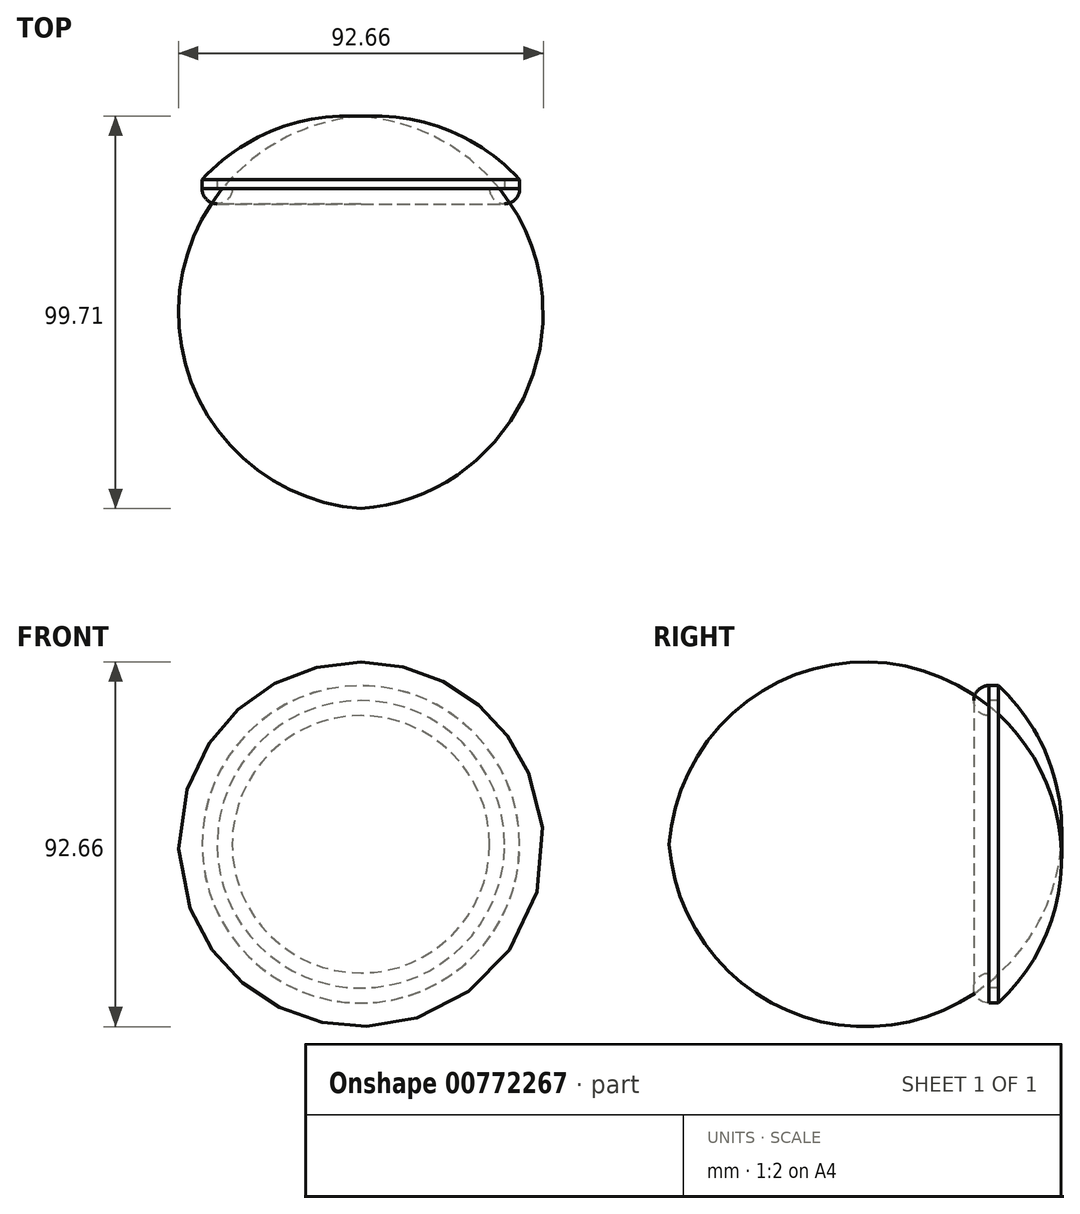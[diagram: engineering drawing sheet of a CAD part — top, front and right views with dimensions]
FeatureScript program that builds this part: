
annotation { "Feature Type Name" : "Feature", "Feature Type Description" : "" }
export const myFeature = defineFeature(function(context is Context, id is Id, definition is map)
    precondition{}
    {
        {
            var Q0;
            Q0=qCreatedBy(makeId("Top.planeOp"),FACE);
            var sketch = newSketch(context, id + "F0", { "sketchPlane" : qUnion([Q0])});
            skLineSegment(sketch, "E0", {"start": v(40.32, 0) * mm, "end": v(0, 0) * mm});
            skLineSegment(sketch, "E1", {"start": v(0, 0) * mm, "end": v(0, 15.98) * mm});
            skArc(sketch, "E2", {"start": v(40.32, 0) * mm, "mid": v(21.98, 12.6) * mm, "end": v(0, 15.98) * mm});
            skLineSegment(sketch, "E3", {"start": v(36.52, 0) * mm, "end": v(36.52, -2.4) * mm});
            skLineSegment(sketch, "E4", {"start": v(36.52, -2.4) * mm, "end": v(32.7, -2.4) * mm});
            skArc(sketch, "E5", {"start": v(32.7, -2.4) * mm, "mid": v(36.52, -6.21) * mm, "end": v(40.34, -2.4) * mm});
            skLineSegment(sketch, "E6", {"start": v(40.32, 0) * mm, "end": v(40.34, -2.4) * mm});
            skSolve(sketch);
        }
        {
            var Q0;
            Q0 = qSketchRegion(id + "F0", true);
            var Q1;
            Q1=sQuery(id+"F0.wireOp",EDGE,"E1");
            revolve(context, id + "F1", {"surfaceOperationType" : NewSurfaceOperationType.NEW, "entities" : qUnion([Q0]), "axis" : qUnion([Q1]), "revolveType" : RevolveType.FULL});
        }
    });
